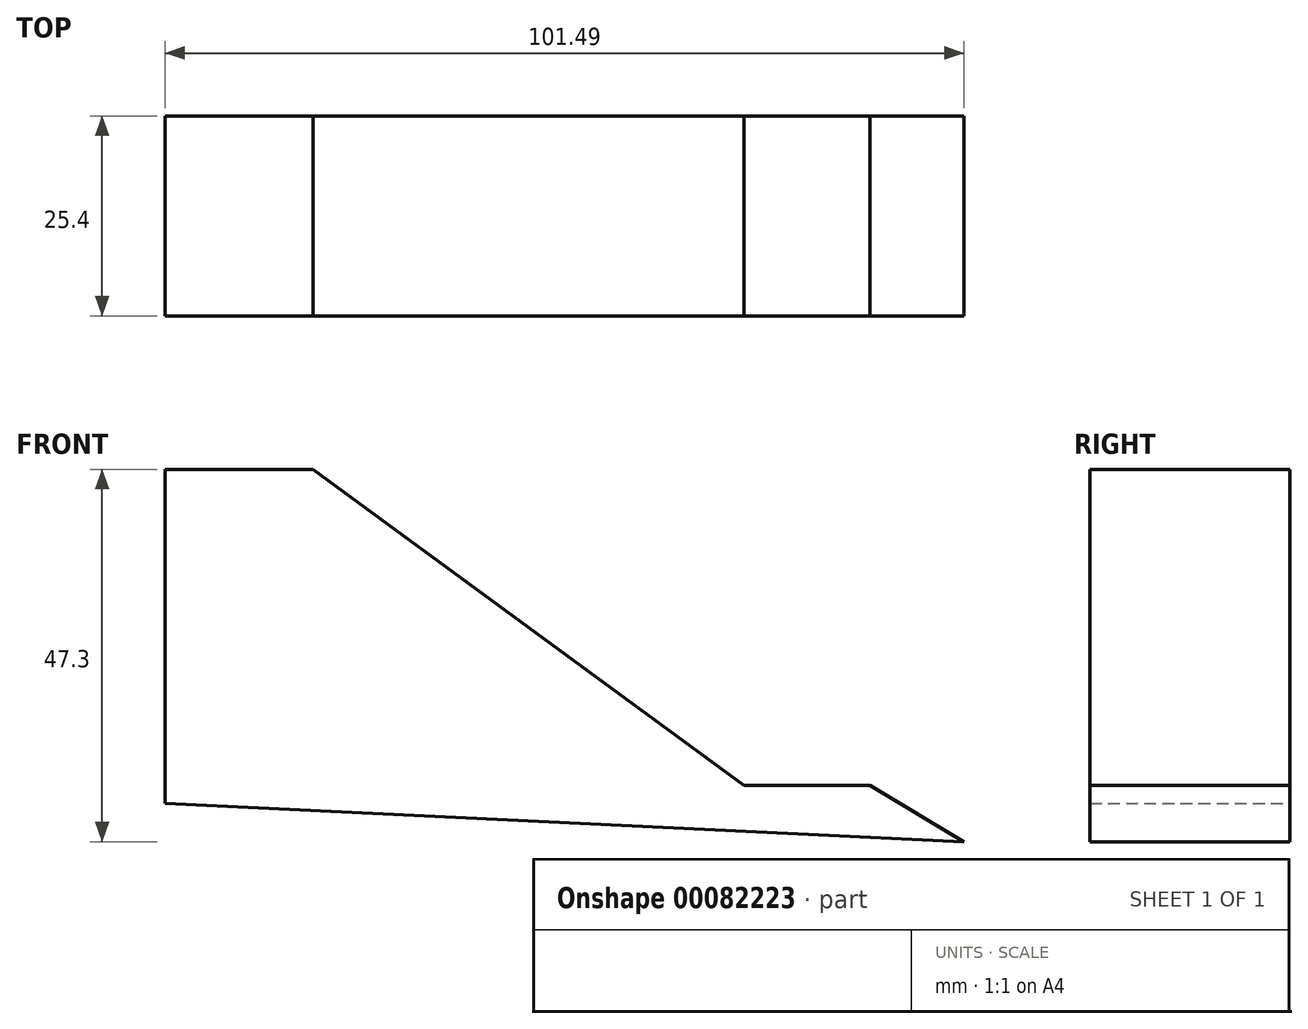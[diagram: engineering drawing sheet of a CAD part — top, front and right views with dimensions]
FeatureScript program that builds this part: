
annotation { "Feature Type Name" : "Feature", "Feature Type Description" : "" }
export const myFeature = defineFeature(function(context is Context, id is Id, definition is map)
    precondition{}
    {
        {
            var Q0;
            Q0=qCreatedBy(makeId("Front.planeOp"),FACE);
            var sketch = newSketch(context, id + "F0", { "sketchPlane" : qUnion([Q0])});
            skLineSegment(sketch, "E0", {"start": v(-45.11, -34.39) * mm, "end": v(-45.11, 8.07) * mm});
            skLineSegment(sketch, "E1", {"start": v(-45.11, 8.07) * mm, "end": v(-26.29, 8.07) * mm});
            skLineSegment(sketch, "E2", {"start": v(-26.29, 8.07) * mm, "end": v(28.45, -32.08) * mm});
            skLineSegment(sketch, "E3", {"start": v(28.45, -32.08) * mm, "end": v(44.41, -32.08) * mm});
            skLineSegment(sketch, "E4", {"start": v(44.41, -32.08) * mm, "end": v(56.38, -39.23) * mm});
            skLineSegment(sketch, "E5", {"start": v(56.38, -39.23) * mm, "end": v(-45.11, -34.39) * mm});
            skSolve(sketch);
        }
        {
            var Q0;
            Q0=makeQuery(id+"F0.imprint","IMPRINT",FACE,{"disambiguationData":[TD([[makeQuery(id+"F0.imprint","IMPRINT",EDGE,{"derivedFrom":sQuery(id+"F0.wireOp",EDGE,"E0")}),-1.0]])]});
            extrude(context, id + "F1", {"entities" : qUnion([Q0]), "depth" : 25.4 * mm});
        }
    });
